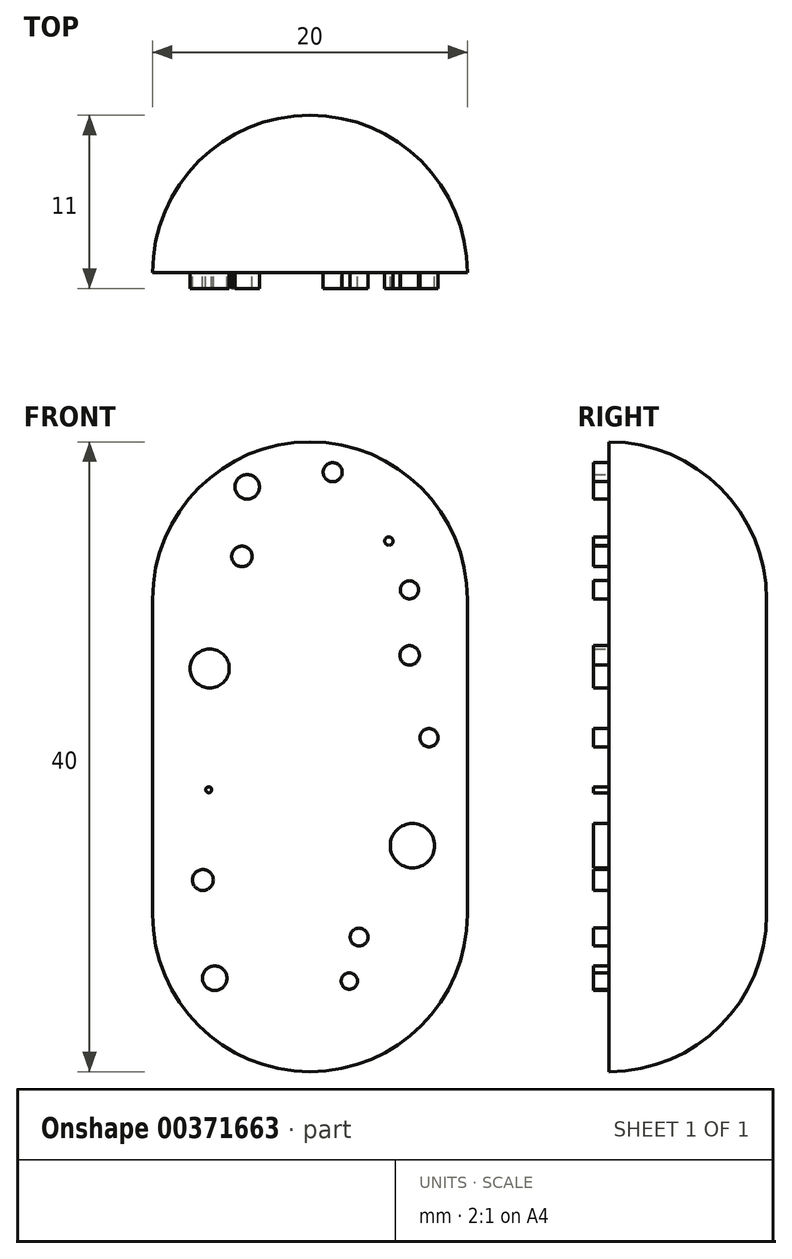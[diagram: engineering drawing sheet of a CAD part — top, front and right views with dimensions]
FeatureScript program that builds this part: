
annotation { "Feature Type Name" : "Feature", "Feature Type Description" : "" }
export const myFeature = defineFeature(function(context is Context, id is Id, definition is map)
    precondition{}
    {
        {
            var Q0;
            Q0=qCreatedBy(makeId("Front.planeOp"),FACE);
            var sketch = newSketch(context, id + "F0", { "sketchPlane" : qUnion([Q0])});
            skLineSegment(sketch, "E0.bottom", {"start": v(0, 0) * mm, "end": v(10, 0) * mm});
            skLineSegment(sketch, "E0.top", {"start": v(0, 20) * mm, "end": v(10, 20) * mm});
            skLineSegment(sketch, "E0.left", {"start": v(0, 0) * mm, "end": v(0, 20) * mm});
            skArc(sketch, "E1", {"start": v(10, 30) * mm, "mid": v(2.93, 27.07) * mm, "end": v(0, 20) * mm});
            skArc(sketch, "E2", {"start": v(0, 0) * mm, "mid": v(2.93, -7.07) * mm, "end": v(10, -10) * mm});
            skLineSegment(sketch, "E3", {"start": v(10, 30) * mm, "end": v(10, -10) * mm});
            skSolve(sketch);
        }
        {
            var Q0;
            Q0 = qSketchRegion(id + "F0", true);
            var Q1;
            Q1=sQuery(id+"F0.wireOp",EDGE,"E3");
            revolve(context, id + "F1", {"entities" : qUnion([Q0]), "axis" : qUnion([Q1]), "revolveType" : RevolveType.ONE_DIRECTION, "angle" : 180 * degree});
        }
        {
            var Q0;
            Q0=makeQuery(id+"F1.opRevolve","CAP_FACE",FACE,{"disambiguationData":[OSD([sQuery(id+"F0.wireOp",EDGE,"E0.left"),sQuery(id+"F0.wireOp",EDGE,"E1"),sQuery(id+"F0.wireOp",EDGE,"E2"),sQuery(id+"F0.wireOp",EDGE,"E3")])],"isStart":true});
            var sketch = newSketch(context, id + "F2", { "sketchPlane" : qUnion([Q0])});
            skCircle(sketch, "E4", {"center": v(5.68, 22.73) * mm, "radius": 0.65 * mm});
            skCircle(sketch, "E5", {"center": v(16.31, 20.6) * mm, "radius": 0.58 * mm});
            skCircle(sketch, "E6", {"center": v(3.63, 15.6) * mm, "radius": 1.24 * mm});
            skCircle(sketch, "E7", {"center": v(16.5, 4.35) * mm, "radius": 1.4 * mm});
            skCircle(sketch, "E8", {"center": v(3.57, 7.9) * mm, "radius": 0.19 * mm});
            skCircle(sketch, "E9", {"center": v(16.33, 16.44) * mm, "radius": 0.62 * mm});
            skCircle(sketch, "E10", {"center": v(3.95, -4.06) * mm, "radius": 0.78 * mm});
            skCircle(sketch, "E11", {"center": v(3.2, 2.17) * mm, "radius": 0.66 * mm});
            skCircle(sketch, "E12", {"center": v(11.44, 28.08) * mm, "radius": 0.6 * mm});
            skCircle(sketch, "E13", {"center": v(6.01, 27.15) * mm, "radius": 0.78 * mm});
            skCircle(sketch, "E14", {"center": v(15, 23.7) * mm, "radius": 0.27 * mm});
            skCircle(sketch, "E15", {"center": v(12.5, -4.25) * mm, "radius": 0.52 * mm});
            skCircle(sketch, "E16", {"center": v(13.12, -1.45) * mm, "radius": 0.57 * mm});
            skCircle(sketch, "E17", {"center": v(17.56, 11.21) * mm, "radius": 0.58 * mm});
            skSolve(sketch);
        }
        {
            var Q0;
            Q0 = qSketchRegion(id + "F2", true);
            var Q1;
            Q1=sQuery(id+"F2.wireOp",EDGE,"E4");
            extrude(context, id + "F3", {"entities" : qUnion([Q0]), "bodyType" : ToolBodyType.SURFACE, "surfaceEntities" : qUnion([Q1]), "depth" : 1 * mm});
        }
        {
            var Q0;
            Q0 = qSketchRegion(id + "F2", true);
            extrude(context, id + "F4", {"entities" : qUnion([Q0]), "operationType" : NewBodyOperationType.ADD, "depth" : 1 * mm});
        }
        {
            var Q0;
            Q0=makeQuery(id+"F1.opRevolve","CAP_FACE",FACE,{"disambiguationData":[OSD([sQuery(id+"F0.wireOp",EDGE,"E0.left"),sQuery(id+"F0.wireOp",EDGE,"E1"),sQuery(id+"F0.wireOp",EDGE,"E2"),sQuery(id+"F0.wireOp",EDGE,"E3")])],"isStart":true});
            var sketch = newSketch(context, id + "F5", { "sketchPlane" : qUnion([Q0])});
            skFitSpline(sketch, "E18", {"points": [v(11.04, -1.97) * mm, v(11, -5.49) * mm, v(13.85, -5.06) * mm, v(14.1, -0.68) * mm, v(11.04, -1.97) * mm]});
            skSolve(sketch);
        }
        {
            var Q0;
            Q0 = qSketchRegion(id + "F5", true);
            var Q1;
            Q1=sQuery(id+"F5.wireOp",EDGE,"E18");
            extrude(context, id + "F6", {"entities" : qUnion([Q0]), "bodyType" : ToolBodyType.SURFACE, "surfaceEntities" : qUnion([Q1]), "depth" : 1 * mm});
        }
        {
            var Q0;
            Q0=makeQuery(id+"F1.opRevolve","CAP_FACE",FACE,{"disambiguationData":[OSD([sQuery(id+"F0.wireOp",EDGE,"E0.left"),sQuery(id+"F0.wireOp",EDGE,"E1"),sQuery(id+"F0.wireOp",EDGE,"E2"),sQuery(id+"F0.wireOp",EDGE,"E3")])],"isStart":true});
            var sketch = newSketch(context, id + "F7", { "sketchPlane" : qUnion([Q0])});
            skFitSpline(sketch, "E19", {"points": [v(8.9, 20.74) * mm, v(7.56, 16.82) * mm, v(9.53, 14.29) * mm, v(6.65, 10.11) * mm, v(10, 6.18) * mm, v(7.55, 1.62) * mm, v(7.85, 5.57) * mm, v(4.85, 9.89) * mm, v(7.65, 14.75) * mm, v(4.97, 18.22) * mm, v(10.86, 23.12) * mm, v(8.5, 17.1) * mm, v(12.2, 17.69) * mm, v(8.33, 10.26) * mm, v(12.23, 8.25) * mm, v(10.2, 3.67) * mm, v(14.24, 7.54) * mm, v(11.09, 10.43) * mm, v(12.67, 15.3) * mm, v(14.1, 18.6) * mm, v(10.1, 18.37) * mm, v(11.9, 21.77) * mm, v(13.18, 22.02) * mm], "startDerivative": vector(-65.5, -100.28) * mm, "endDerivative": vector(45.73, -9.64) * mm});
            skSolve(sketch);
        }
        {
            var Q0;
            Q0 = qSketchRegion(id + "F7", true);
            var Q1;
            Q1=sQuery(id+"F7.wireOp",EDGE,"E19");
            extrude(context, id + "F8", {"entities" : qUnion([Q0]), "bodyType" : ToolBodyType.SURFACE, "surfaceEntities" : qUnion([Q1]), "depth" : 1 * mm});
        }
        {
            var Q0;
            Q0=qCreatedBy(makeId("Front.planeOp"),FACE);
            var sketch = newSketch(context, id + "F9", { "sketchPlane" : qUnion([Q0])});
            skFitSpline(sketch, "E20", {"points": [v(9.76, -9.16) * mm, v(12.22, -13.26) * mm, v(6.9, -17.56) * mm, v(8.64, -25.32) * mm, v(11.07, -19.84) * mm], "startDerivative": vector(20.73, -21.03) * mm, "endDerivative": vector(8.45, 35.96) * mm});
            skSolve(sketch);
        }
        {
            var Q0;
            Q0=sQuery(id+"F9.wireOp",EDGE,"E20");
            extrude(context, id + "F10", {"bodyType" : ToolBodyType.SURFACE, "surfaceEntities" : qUnion([Q0]), "depth" : 1 * mm});
        }
    });
